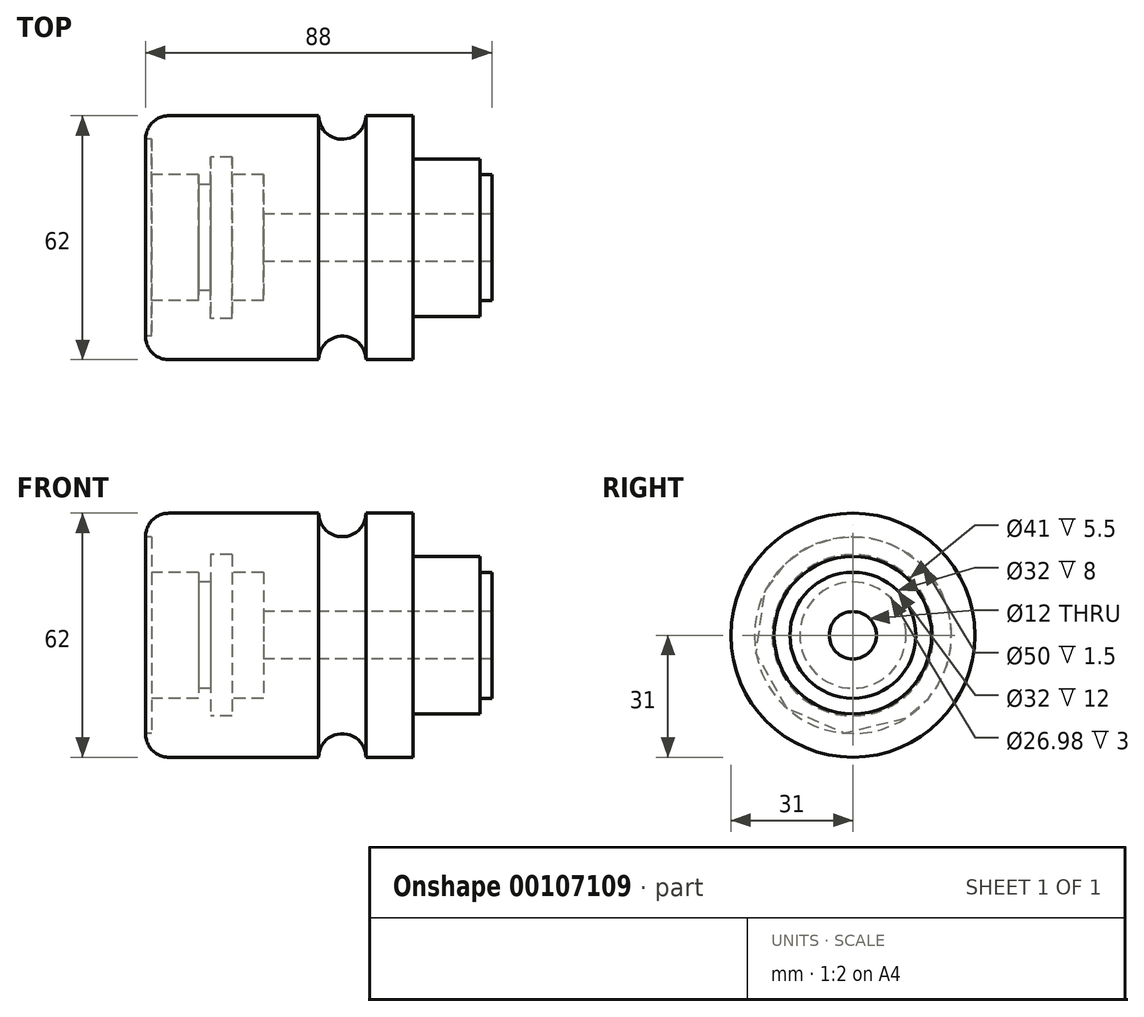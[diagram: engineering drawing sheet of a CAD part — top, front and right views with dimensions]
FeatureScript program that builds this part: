
annotation { "Feature Type Name" : "Feature", "Feature Type Description" : "" }
export const myFeature = defineFeature(function(context is Context, id is Id, definition is map)
    precondition{}
    {
        {
            var Q0;
            Q0=qCreatedBy(makeId("Top.planeOp"),FACE);
            var sketch = newSketch(context, id + "F0", { "sketchPlane" : qUnion([Q0])});
            skLineSegment(sketch, "E0", {"start": v(-105.89, 0) * mm, "end": v(25.72, 0) * mm, "construction": true});
            skLineSegment(sketch, "E1", {"start": v(25.72, 0) * mm, "end": v(25.72, 6) * mm, "construction": true});
            skLineSegment(sketch, "E2", {"start": v(25.72, 6) * mm, "end": v(25.72, 16) * mm});
            skLineSegment(sketch, "E3", {"start": v(25.72, 16) * mm, "end": v(22.72, 16) * mm});
            skLineSegment(sketch, "E4", {"start": v(22.72, 16) * mm, "end": v(22.72, 20) * mm});
            skLineSegment(sketch, "E5", {"start": v(22.72, 20) * mm, "end": v(5.72, 20) * mm});
            skLineSegment(sketch, "E6", {"start": v(5.72, 20) * mm, "end": v(5.72, 31) * mm});
            skLineSegment(sketch, "E7", {"start": v(5.72, 31) * mm, "end": v(-6.28, 31) * mm});
            skLineSegment(sketch, "E8", {"start": v(-6.28, 31) * mm, "end": v(-18.28, 31) * mm, "construction": true});
            skArc(sketch, "E9", {"start": v(-18.28, 31) * mm, "mid": v(-12.28, 25.02) * mm, "end": v(-6.28, 31) * mm});
            skLineSegment(sketch, "E10", {"start": v(-18.28, 31) * mm, "end": v(-62.28, 31) * mm});
            skLineSegment(sketch, "E11", {"start": v(-60.78, 25) * mm, "end": v(-62.28, 25) * mm});
            skLineSegment(sketch, "E12", {"start": v(-62.28, 25) * mm, "end": v(-62.28, 31) * mm});
            skLineSegment(sketch, "E13", {"start": v(-48.78, 16) * mm, "end": v(-60.78, 16) * mm});
            skLineSegment(sketch, "E14", {"start": v(-45.78, 20.5) * mm, "end": v(-40.28, 20.5) * mm});
            skLineSegment(sketch, "E15", {"start": v(-48.78, 13.49) * mm, "end": v(-45.78, 13.49) * mm});
            skLineSegment(sketch, "E16", {"start": v(-32.28, 16) * mm, "end": v(-40.28, 16) * mm});
            skLineSegment(sketch, "E17", {"start": v(-32.28, 6) * mm, "end": v(-32.28, 16) * mm});
            skLineSegment(sketch, "E18", {"start": v(-48.78, 16) * mm, "end": v(-48.78, 13.49) * mm});
            skLineSegment(sketch, "E19", {"start": v(-45.78, 20.5) * mm, "end": v(-45.78, 13.49) * mm});
            skLineSegment(sketch, "E20", {"start": v(-40.28, 20.5) * mm, "end": v(-40.28, 16) * mm});
            skLineSegment(sketch, "E21", {"start": v(-32.28, 6) * mm, "end": v(25.72, 6) * mm});
            skLineSegment(sketch, "E22", {"start": v(-60.78, 16) * mm, "end": v(-60.78, 25) * mm});
            skSolve(sketch);
        }
        {
            var Q0;
            Q0=makeQuery(id+"F0.imprint","IMPRINT",FACE,{"disambiguationData":[TD([[makeQuery(id+"F0.imprint","IMPRINT",EDGE,{"derivedFrom":sQuery(id+"F0.wireOp",EDGE,"E2")}),1.0]])]});
            var Q1;
            Q1=sQuery(id+"F0.wireOp",EDGE,"E0");
            revolve(context, id + "F1", {"entities" : qUnion([Q0]), "axis" : qUnion([Q1]), "revolveType" : RevolveType.FULL});
        }
        {
            var Q0;
            Q0=makeQuery(id+"F1.opRevolve","SWEPT_EDGE",EDGE,{"disambiguationData":[OSD([sQuery(id+"F0.wireOp",EDGE,"E10"),sQuery(id+"F0.wireOp",EDGE,"E12")])]});
            fillet(context, id + "F2", {"entities" : qUnion([Q0]), "radius" : 6 * mm, "tangentPropagation" : true, "allowEdgeOverflow" : false});
        }
    });
